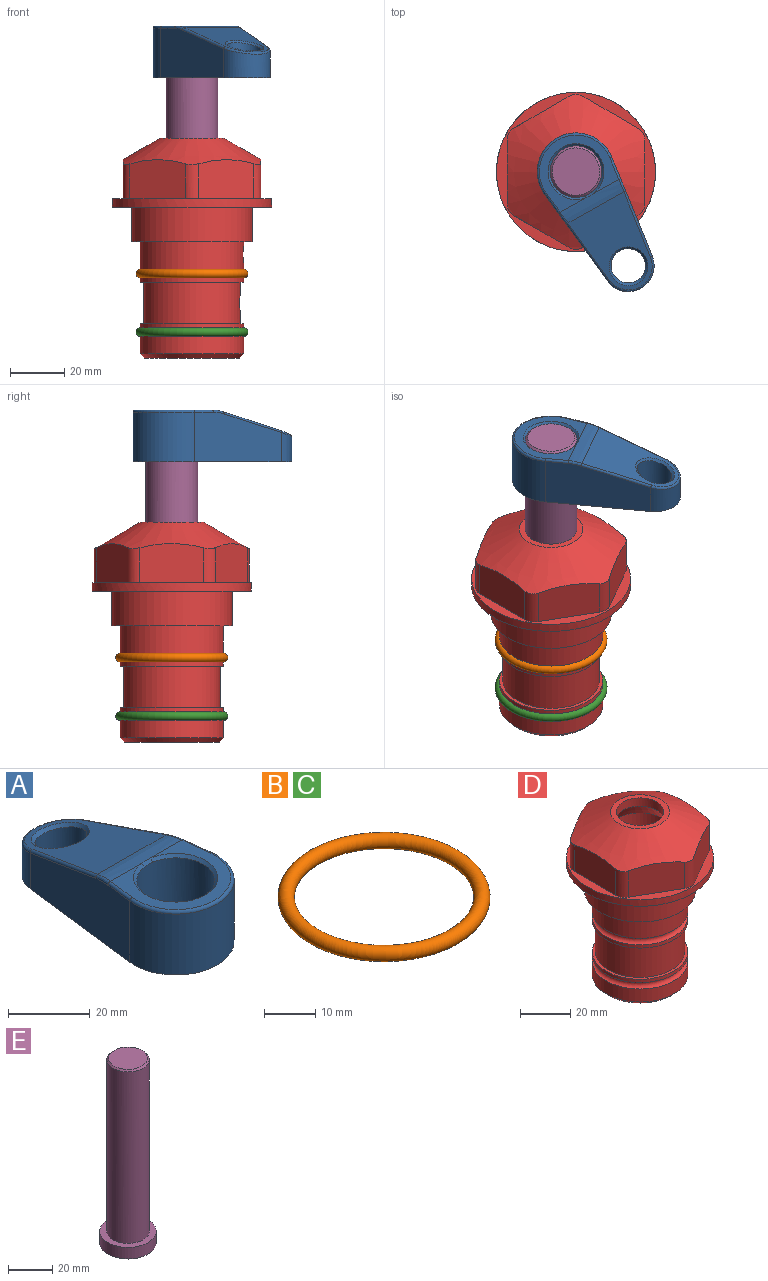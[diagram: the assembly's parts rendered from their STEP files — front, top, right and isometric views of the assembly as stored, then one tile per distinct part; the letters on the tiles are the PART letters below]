
ASSEMBLY  parts=5 mates=4
PART A: 31 faces, bbox 31.7x65.5x19.8 mm
  f0: plane 39.12x18.26mm, normal (0.99,0.12,0), area 612.2mm2, adj f1,f4,f7,f11,f13,f15
  f1: cylinder r=9.53mm len=18.91mm, axis (0,0,-1), area 296.1mm2, adj f0,f2,f7,f17
  f2: plane 39.12x18.26mm, normal (-0.99,0.12,0), area 612.2mm2, adj f1,f4,f7,f12,f14,f16
  f3: cylinder r=6.35mm len=12.7mm, axis (0,0,-1), area 362.4mm2, adj f7,f18
  f4: cylinder r=14.29mm len=28.58mm, axis (0,0,-1), area 882.2mm2, adj f0,f2,f7,f10
  f5: cylinder r=9.53mm len=19.05mm, axis (0,0,-1), area 1092.6mm2, adj f7,f19,f20
  f6: plane 26.99x23.69mm, normal (0,0,1), area 216.2mm2, adj f9,f10,f11,f12,f19
  f7: plane 63.5x28.58mm, normal (0,0,-1), area 661.8mm2, adj f0,f1,f2,f3,f4,f5,f22,f23
  f8: plane 33.52x23.6mm, normal (0,0.26,0.97), area 486mm2, adj f9,f15,f16,f17,f18
  f9: cylinder r=19.05mm len=24.72mm, axis (1,0,0), area 120.4mm2, adj f6,f8,f13,f14,f20
  f10: torus R=13.49mm, axis (0,0,1), area 59mm2, adj f4,f6,f11,f12
  f11: cylinder r=0.79mm len=8.67mm, axis (0.12,-0.99,0), area 10.8mm2, adj f0,f6,f10,f13
  f12: cylinder r=0.79mm len=8.67mm, axis (0.12,0.99,0), area 10.8mm2, adj f2,f6,f10,f14
  f13: bspline ~4.95x1.42mm, area 6.1mm2, adj f0,f9,f11,f15
  f14: bspline ~4.95x1.42mm, area 6.1mm2, adj f2,f9,f12,f16
  f15: cylinder r=0.79mm len=25.95mm, axis (0.12,-0.96,0.26), area 32.9mm2, adj f0,f8,f13,f17
  f16: cylinder r=0.79mm len=25.95mm, axis (0.12,0.96,-0.26), area 32.9mm2, adj f2,f8,f14,f17
  f17: bspline ~18.91x8.38mm, area 30mm2, adj f1,f8,f15,f16
  f18: bspline ~14.29x14.29mm, area 48.3mm2, adj f3,f8
  f19: cone r=9.53mm half-angle=45deg, axis (0,0,1), area 66.5mm2, adj f5,f6,f20
  f20: bspline ~3.22x0.96mm, area 3.5mm2, adj f5,f9,f19
  f21: plane 2.75x2.72mm, normal (0,0,-1), area 2.9mm2, adj f23,f25,f28
  f22: plane 23.05x15.88mm, normal (-0.99,-0.12,0), area 323.6mm2, adj f7,f25,f26,f27,f28,f29
  f23: plane 23.05x15.88mm, normal (0.99,-0.12,0), area 323.6mm2, adj f7,f21,f25,f27,f28,f30
  f24: cylinder r=9.53mm len=10.69mm, axis (0,0,-1), area 114.7mm2, adj f7,f27,f29,f30
  f25: cylinder r=12.7mm len=20.59mm, axis (0,0,-1), area 381.1mm2, adj f7,f21,f22,f23,f26,f28
  f26: plane 2.75x2.72mm, normal (0,0,-1), area 2.9mm2, adj f22,f25,f28
  f27: plane 19.72x18.37mm, normal (0,-0.26,-0.97), area 291.8mm2, adj f22,f23,f24,f28,f29,f30
  f28: cylinder r=15.88mm len=19.92mm, axis (1,0,0), area 54.8mm2, adj f21,f22,f23,f25,f26,f27
  f29: cylinder r=1.59mm len=11mm, axis (0,0,-1), area 34.7mm2, adj f7,f22,f24,f27
  f30: cylinder r=1.59mm len=11mm, axis (0,0,-1), area 34.7mm2, adj f7,f23,f24,f27
PART B: 1 faces, bbox 44.7x44.7x3.2 mm
  f0: torus R=19.05mm, axis (0,0,1), area 1193.9mm2
PART C: same geometry as B
PART D: 36 faces, bbox 58.7x58.7x81 mm
  f0: cylinder r=17.78mm len=35.56mm, axis (0,0,1), area 1670.8mm2, adj f23,f24,f31
  f1: cylinder r=19.05mm len=38.1mm, axis (0,0,1), area 1191.9mm2, adj f26,f27,f30
  f2: plane 58.66x58.66mm, normal (0,0,-1), area 1150.6mm2, adj f3,f28
  f3: cylinder r=29.33mm len=58.66mm, axis (0,0,-1), area 585.1mm2, adj f2,f4
  f4: plane 58.66x58.66mm, normal (0,0,1), area 475.9mm2, adj f3,f5,f6,f7,f8,f9,f10,f11
  f5: plane 20.32x14.34mm, normal (-0.5,0.87,0), area 324.4mm2, adj f4,f15,f16,f17
  f6: plane 20.32x14.34mm, normal (0.5,0.87,0), area 324.4mm2, adj f4,f14,f15,f17
  f7: plane 23.48x14.34mm, normal (1,0,0), area 324.4mm2, adj f4,f13,f14,f17
  f8: plane 20.32x14.34mm, normal (0.5,-0.87,0), area 324.4mm2, adj f4,f12,f13,f17
  f9: plane 20.32x14.34mm, normal (-0.5,-0.87,0), area 324.4mm2, adj f4,f11,f12,f17
  f10: plane 23.48x14.34mm, normal (-1,0,0), area 324.4mm2, adj f4,f11,f16,f17
  f11: cylinder r=5.08mm len=12.85mm, axis (0,0,-1), area 67.2mm2, adj f4,f9,f10,f17
  f12: cylinder r=5.08mm len=12.85mm, axis (0,0,-1), area 67.2mm2, adj f4,f8,f9,f17
  f13: cylinder r=5.08mm len=12.85mm, axis (0,0,-1), area 67.2mm2, adj f4,f7,f8,f17
  f14: cylinder r=5.08mm len=12.85mm, axis (0,0,-1), area 67.2mm2, adj f4,f6,f7,f17
  f15: cylinder r=5.08mm len=12.85mm, axis (0,0,-1), area 67.2mm2, adj f4,f5,f6,f17
  f16: cylinder r=5.08mm len=12.85mm, axis (0,0,-1), area 67.2mm2, adj f4,f5,f10,f17
  f17: cone r=11.73mm half-angle=60deg, axis (0,0,-1), area 2071.8mm2, adj f5,f6,f7,f8,f9,f10,f11,f12
  f18: plane 23.46x23.46mm, normal (0,0,1), area 147.4mm2, adj f17,f35
  f19: plane 34.93x34.93mm, normal (0,0,-1), area 958mm2, adj f29
  f20: cylinder r=19.05mm len=38.1mm, axis (0,0,1), area 760.1mm2, adj f21,f29
  f21: torus R=19.05mm, axis (0,0,1), area 565.3mm2, adj f20,f22
  f22: cylinder r=19.05mm len=38.1mm, axis (0,0,1), area 190mm2, adj f21,f23
  f23: plane 38.1x38.1mm, normal (0,0,1), area 146.9mm2, adj f0,f22
  f24: plane 38.1x38.1mm, normal (0,0,-1), area 146.9mm2, adj f0,f25
  f25: cylinder r=19.05mm len=38.1mm, axis (0,0,1), area 190mm2, adj f24,f26
  f26: torus R=19.05mm, axis (0,0,1), area 565.3mm2, adj f1,f25
  f27: plane 44.45x44.45mm, normal (0,0,-1), area 411.7mm2, adj f1,f28
  f28: cylinder r=22.23mm len=44.45mm, axis (0,0,1), area 1773.5mm2, adj f2,f27
  f29: cone r=19.05mm half-angle=45deg, axis (0,0,1), area 257.5mm2, adj f19,f20
  f30: cylinder r=3.17mm len=6.75mm, axis (-1,0,0), area 128mm2, adj f1,f33
  f31: cylinder r=3.17mm len=6.35mm, axis (-1,0,0), area 102.5mm2, adj f0,f33
  f32: plane 25.4x25.4mm, normal (0,0,1), area 506.7mm2, adj f33
  f33: cylinder r=12.7mm len=66.42mm, axis (0,0,-1), area 5236.2mm2, adj f30,f31,f32,f34
  f34: cone r=9.53mm half-angle=30deg, axis (0,0,-1), area 443.4mm2, adj f33,f35
  f35: cylinder r=9.53mm len=19.05mm, axis (0,0,-1), area 240.9mm2, adj f18,f34
PART E: 6 faces, bbox 25.4x25.4x101.6 mm
  f0: plane 17.46x17.46mm, normal (0,0,1), area 239.5mm2, adj f5
  f1: plane 25.4x25.4mm, normal (0,0,-1), area 506.7mm2, adj f2
  f2: cylinder r=12.7mm len=25.4mm, axis (0,0,1), area 506.7mm2, adj f1,f3
  f3: plane 25.4x25.4mm, normal (0,0,1), area 221.7mm2, adj f2,f4
  f4: cylinder r=9.53mm len=94.46mm, axis (0,0,1), area 5653mm2, adj f3,f5
  f5: cone r=8.73mm half-angle=45deg, axis (0,0,-1), area 64.4mm2, adj f0,f4
PLACE A rot(axis=(0,0,-1),150.9deg) t=(0,0,3.28)mm
PLACE B at identity
PLACE C t=(0,0,-21.59)mm
PLACE D at identity fixed
PLACE E rot(axis=(0,0,-1),150.9deg) t=(0,0,3.28)mm
MATE fastened B.f0 <-> D.f0  axis (0,0,1) through (0,0,-24.51)mm
MATE fastened C.f0 <-> D.f0  axis (0,0,1) through (0,0,-46.1)mm
MATE cylindrical E.f2 <-> D.f0  axis (0,0,-1) through (0,0,-34.82)mm
MATE fastened A.f4 <-> E.f2  axis (0,0,1) through (0,0,66.78)mm
